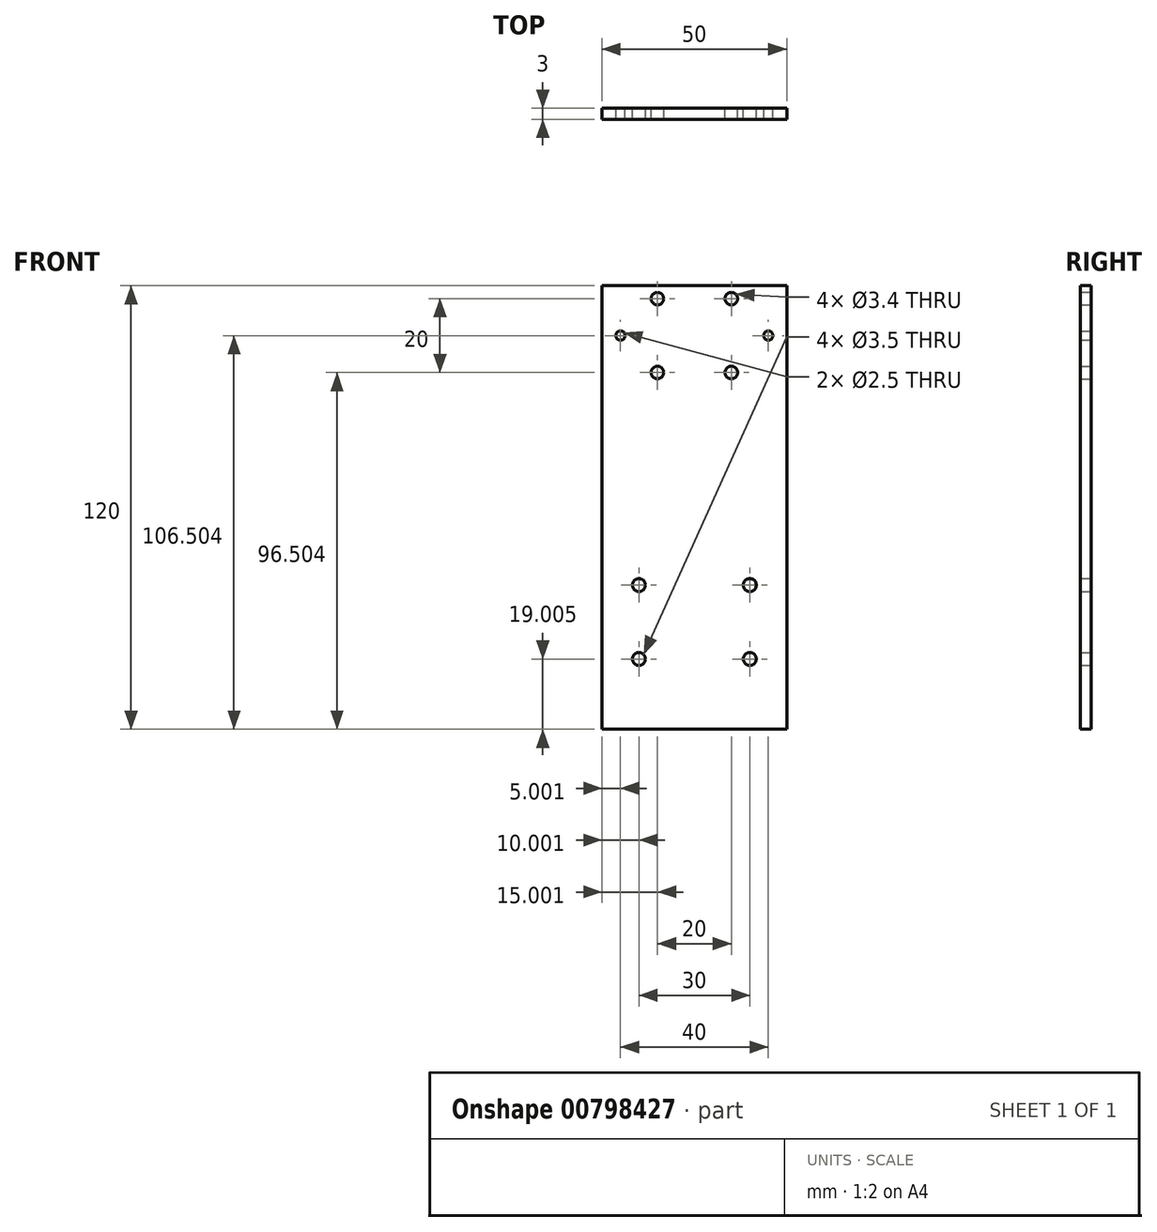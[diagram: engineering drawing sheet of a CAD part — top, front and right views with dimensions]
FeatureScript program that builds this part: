
annotation { "Feature Type Name" : "Feature", "Feature Type Description" : "" }
export const myFeature = defineFeature(function(context is Context, id is Id, definition is map)
    precondition{}
    {
        {
            var Q0;
            Q0=qCreatedBy(makeId("Front.planeOp"),FACE);
            var sketch = newSketch(context, id + "F0", { "sketchPlane" : qUnion([Q0])});
            skLineSegment(sketch, "E0.bottom", {"start": v(-30.5, 123.6) * mm, "end": v(19.5, 123.6) * mm});
            skLineSegment(sketch, "E0.top", {"start": v(-30.5, -26.4) * mm, "end": v(19.5, -26.4) * mm});
            skLineSegment(sketch, "E0.left", {"start": v(-30.5, 123.6) * mm, "end": v(-30.5, -26.4) * mm});
            skLineSegment(sketch, "E0.right", {"start": v(19.5, 123.6) * mm, "end": v(19.5, -26.4) * mm});
            skLineSegment(sketch, "E1", {"start": v(-30.5, 120.1) * mm, "end": v(19.5, 120.1) * mm, "construction": true});
            skLineSegment(sketch, "E2", {"start": v(-30.5, 100.1) * mm, "end": v(19.5, 100.1) * mm, "construction": true});
            skLineSegment(sketch, "E3", {"start": v(-5.5, -26.4) * mm, "end": v(-5.5, 123.6) * mm, "construction": true});
            skLineSegment(sketch, "E4", {"start": v(-15.5, 123.6) * mm, "end": v(-15.5, -26.4) * mm, "construction": true});
            skLineSegment(sketch, "E5", {"start": v(4.5, 123.6) * mm, "end": v(4.5, -26.4) * mm, "construction": true});
            skPoint(sketch, "E6", {"position": v(-15.5, 120.1) * mm});
            skPoint(sketch, "E7", {"position": v(4.5, 120.1) * mm});
            skPoint(sketch, "E8", {"position": v(4.5, 100.1) * mm});
            skPoint(sketch, "E9", {"position": v(-15.5, 100.1) * mm});
            skLineSegment(sketch, "E10", {"start": v(19.5, 110.1) * mm, "end": v(-30.5, 110.1) * mm, "construction": true});
            skLineSegment(sketch, "E11", {"start": v(14.5, 123.6) * mm, "end": v(14.5, 100.1) * mm, "construction": true});
            skLineSegment(sketch, "E12", {"start": v(-25.5, 123.6) * mm, "end": v(-25.5, 100.1) * mm, "construction": true});
            skPoint(sketch, "E13", {"position": v(14.5, 110.1) * mm});
            skPoint(sketch, "E14", {"position": v(-25.5, 110.1) * mm});
            skLineSegment(sketch, "E15", {"start": v(-30.5, 22.6) * mm, "end": v(19.5, 22.6) * mm, "construction": true});
            skLineSegment(sketch, "E16", {"start": v(-30.5, 42.6) * mm, "end": v(19.5, 42.6) * mm, "construction": true});
            skLineSegment(sketch, "E17", {"start": v(-20.5, -26.4) * mm, "end": v(-20.5, 123.6) * mm, "construction": true});
            skLineSegment(sketch, "E18", {"start": v(9.5, -26.4) * mm, "end": v(9.5, 123.6) * mm, "construction": true});
            skPoint(sketch, "E19", {"position": v(-20.5, 42.6) * mm});
            skPoint(sketch, "E20", {"position": v(9.5, 42.6) * mm});
            skPoint(sketch, "E21", {"position": v(9.5, 22.6) * mm});
            skPoint(sketch, "E22", {"position": v(-20.5, 22.6) * mm});
            skSolve(sketch);
        }
        {
            var Q0;
            Q0=makeQuery(id+"F0.imprint","IMPRINT",FACE,{"disambiguationData":[TD([[makeQuery(id+"F0.imprint","IMPRINT",EDGE,{"derivedFrom":sQuery(id+"F0.wireOp",EDGE,"E0.bottom")}),-1.0]])]});
            extrude(context, id + "F1", {"entities" : qUnion([Q0]), "depth" : 3 * mm, "offsetDistance" : 25 * mm});
        }
        {
            var Q0;
            Q0=sQuery(id+"F0.wireOp",VERTEX,"E7");
            var Q1;
            Q1=sQuery(id+"F0.wireOp",VERTEX,"E6");
            var Q2;
            Q2=sQuery(id+"F0.wireOp",VERTEX,"E9");
            var Q3;
            Q3=sQuery(id+"F0.wireOp",VERTEX,"E8");
            var Q4;
            Q4=makeQuery(id+"F1.opExtrude","SWEPT_BODY",BODY,{"disambiguationData":[OSD([sQuery(id+"F0.wireOp",EDGE,"E0.bottom"),sQuery(id+"F0.wireOp",EDGE,"E0.top"),sQuery(id+"F0.wireOp",EDGE,"E0.left"),sQuery(id+"F0.wireOp",EDGE,"E0.right")])]});
            hole(context, id + "F2", {"style" : HoleStyle.SIMPLE, "endStyle" : HoleEndStyle.THROUGH, "oppositeDirection" : true, "standardTappedOrClearance" : lookupTablePath({ "fit" : "Normal", "standard" : "ISO", "size" : "M3", "type" : "Clearance" }), "standardBlindInLast" : lookupTablePath({ "fit" : "Normal", "standard" : "ISO", "size" : "M3", "type" : "Clearance" }), "holeDiameter" : 3.4 * mm, "majorDiameter" : 3 * mm, "tappedDepth" : 12 * mm, "tapClearance" : 3, "locations" : qUnion([Q0, Q1, Q2, Q3]), "scope" : qUnion([Q4])});
        }
        {
            var Q0;
            Q0=sQuery(id+"F0.wireOp",VERTEX,"E13");
            var Q1;
            Q1=sQuery(id+"F0.wireOp",VERTEX,"E14");
            var Q2;
            Q2=makeQuery(id+"F1.opExtrude","SWEPT_BODY",BODY,{"disambiguationData":[OSD([sQuery(id+"F0.wireOp",EDGE,"E0.bottom"),sQuery(id+"F0.wireOp",EDGE,"E0.top"),sQuery(id+"F0.wireOp",EDGE,"E0.left"),sQuery(id+"F0.wireOp",EDGE,"E0.right")])]});
            hole(context, id + "F3", {"style" : HoleStyle.SIMPLE, "endStyle" : HoleEndStyle.THROUGH, "oppositeDirection" : true, "standardTappedOrClearance" : lookupTablePath({ "standard" : "ISO", "engagement" : "75%", "pitch" : "0.5 mm", "size" : "M3", "type" : "Tapped" }), "standardBlindInLast" : lookupTablePath({ "standard" : "ISO", "engagement" : "75%", "pitch" : "0.5 mm", "size" : "M3", "type" : "Tapped" }), "holeDiameter" : 2.5 * mm, "majorDiameter" : 3 * mm, "showTappedDepth" : true, "tappedDepth" : 12 * mm, "tapClearance" : 3, "locations" : qUnion([Q0, Q1]), "scope" : qUnion([Q2])});
        }
        {
            var Q0;
            Q0=sQuery(id+"F0.wireOp",VERTEX,"E19");
            var Q1;
            Q1=sQuery(id+"F0.wireOp",VERTEX,"E22");
            var Q2;
            Q2=sQuery(id+"F0.wireOp",VERTEX,"E21");
            var Q3;
            Q3=sQuery(id+"F0.wireOp",VERTEX,"E20");
            var Q4;
            Q4=makeQuery(id+"F1.opExtrude","SWEPT_BODY",BODY,{"disambiguationData":[OSD([sQuery(id+"F0.wireOp",EDGE,"E0.bottom"),sQuery(id+"F0.wireOp",EDGE,"E0.top"),sQuery(id+"F0.wireOp",EDGE,"E0.left"),sQuery(id+"F0.wireOp",EDGE,"E0.right")])]});
            hole(context, id + "F4", {"style" : HoleStyle.SIMPLE, "endStyle" : HoleEndStyle.THROUGH, "oppositeDirection" : true, "standardTappedOrClearance" : lookupTablePath({ "standard" : "ISO", "engagement" : "75%", "pitch" : "0.5 mm", "size" : "M4", "type" : "Tapped" }), "standardBlindInLast" : lookupTablePath({ "standard" : "ISO", "fit" : "Normal", "engagement" : "75%", "pitch" : "0.5 mm", "size" : "M4", "type" : "Clearance & tapped" }), "holeDiameter" : 3.5 * mm, "majorDiameter" : 4 * mm, "showTappedDepth" : true, "tappedDepth" : 12 * mm, "tapClearance" : 3, "locations" : qUnion([Q0, Q1, Q2, Q3]), "scope" : qUnion([Q4])});
        }
        {
            var Q0;
            Q0=makeQuery(id+"F1.opExtrude","SWEPT_FACE",FACE,{"disambiguationData":[OSD([sQuery(id+"F0.wireOp",EDGE,"E0.top")])]});
            extrude(context, id + "F5", {"entities" : qUnion([Q0]), "operationType" : NewBodyOperationType.REMOVE, "oppositeDirection" : true, "depth" : 30 * mm, "offsetDistance" : 25 * mm});
        }
    });
